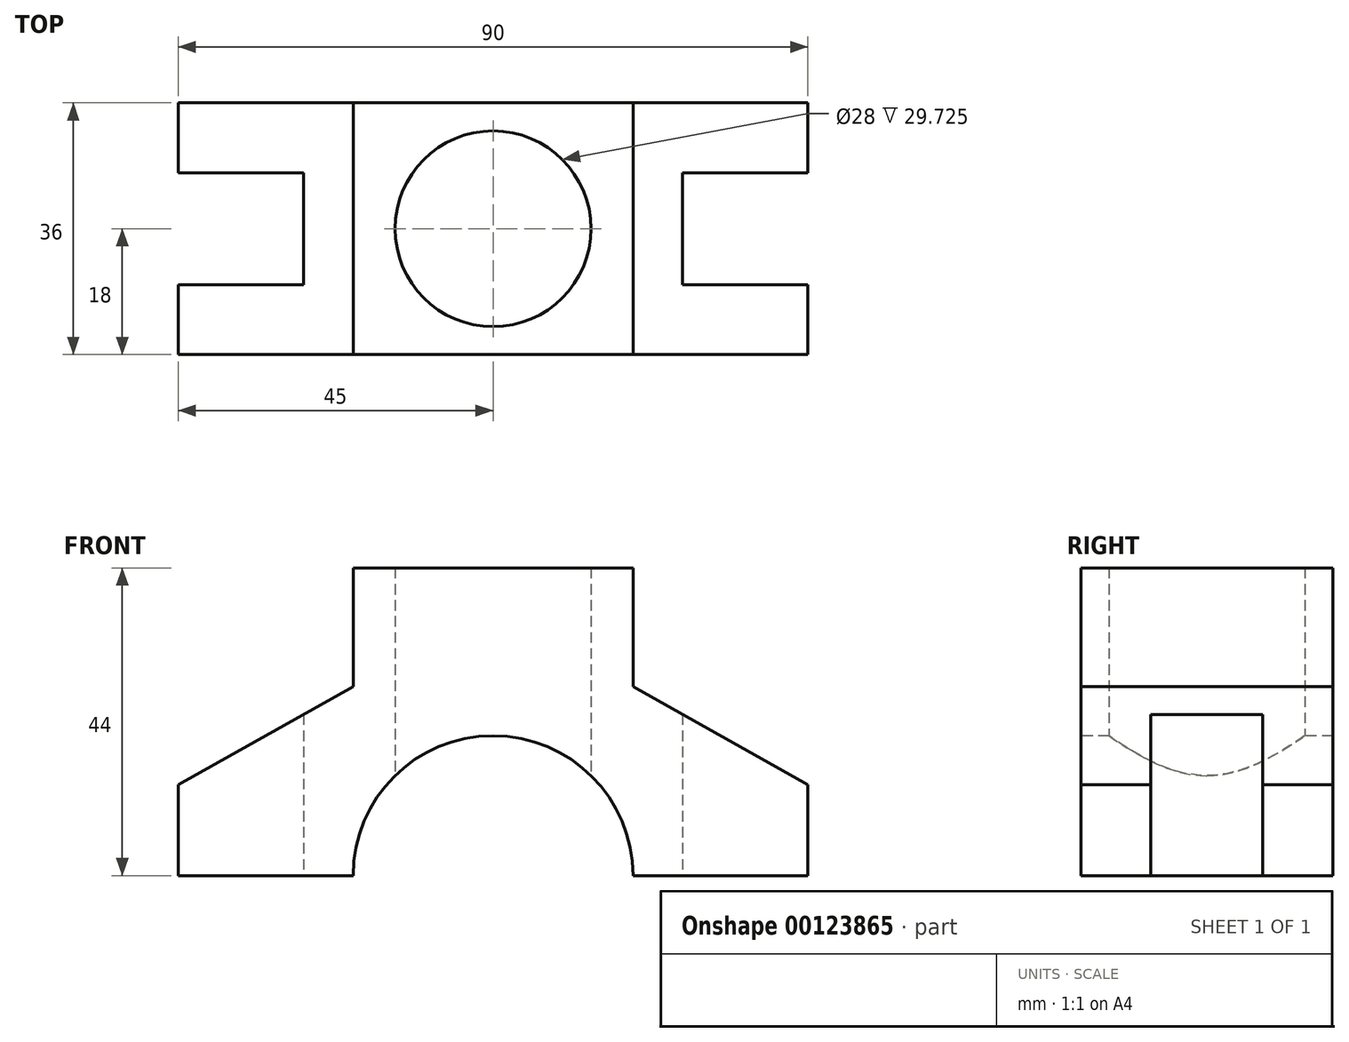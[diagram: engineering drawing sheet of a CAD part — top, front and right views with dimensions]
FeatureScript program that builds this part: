
annotation { "Feature Type Name" : "Feature", "Feature Type Description" : "" }
export const myFeature = defineFeature(function(context is Context, id is Id, definition is map)
    precondition{}
    {
        {
            var Q0;
            Q0=qCreatedBy(makeId("Front.planeOp"),FACE);
            var sketch = newSketch(context, id + "F0", { "sketchPlane" : qUnion([Q0])});
            skLineSegment(sketch, "E0", {"start": v(0, 0) * mm, "end": v(-45, 0) * mm});
            skLineSegment(sketch, "E1", {"start": v(-45, 0) * mm, "end": v(-45, 13) * mm});
            skLineSegment(sketch, "E2", {"start": v(0, 0) * mm, "end": v(0, 44) * mm});
            skLineSegment(sketch, "E3", {"start": v(0, 44) * mm, "end": v(-20, 44) * mm});
            skLineSegment(sketch, "E4", {"start": v(-20, 44) * mm, "end": v(-20, 27) * mm});
            skLineSegment(sketch, "E5", {"start": v(-20, 27) * mm, "end": v(-45, 13) * mm});
            skLineSegment(sketch, "E6.MirrorCS", {"start": v(0, 0) * mm, "end": v(45, 0) * mm});
            skLineSegment(sketch, "E7.MirrorCS", {"start": v(0, 44) * mm, "end": v(20, 44) * mm});
            skLineSegment(sketch, "E8.MirrorCS", {"start": v(45, 0) * mm, "end": v(45, 13) * mm});
            skLineSegment(sketch, "E9.MirrorCS", {"start": v(20, 27) * mm, "end": v(45, 13) * mm});
            skLineSegment(sketch, "E10.MirrorCS", {"start": v(20, 44) * mm, "end": v(20, 27) * mm});
            skSolve(sketch);
        }
        {
            var Q0;
            Q0=makeQuery(id+"F0.imprint","IMPRINT",FACE,{"disambiguationData":[TD([[makeQuery(id+"F0.imprint","IMPRINT",EDGE,{"derivedFrom":sQuery(id+"F0.wireOp",EDGE,"E2")}),-1.0]])]});
            var Q1;
            Q1=makeQuery(id+"F0.imprint","IMPRINT",FACE,{"disambiguationData":[TD([[makeQuery(id+"F0.imprint","IMPRINT",EDGE,{"derivedFrom":sQuery(id+"F0.wireOp",EDGE,"E0")}),-1.0]])]});
            extrude(context, id + "F1", {"entities" : qUnion([Q0, Q1]), "oppositeDirection" : true, "depth" : 36 * mm});
        }
        {
            var Q0;
            Q0=makeQuery(id+"F1.opExtrude","CAP_FACE",FACE,{"disambiguationData":[OSD([sQuery(id+"F0.wireOp",EDGE,"E0"),sQuery(id+"F0.wireOp",EDGE,"E1"),sQuery(id+"F0.wireOp",EDGE,"E3"),sQuery(id+"F0.wireOp",EDGE,"E4"),sQuery(id+"F0.wireOp",EDGE,"E5"),sQuery(id+"F0.wireOp",EDGE,"E6.MirrorCS"),sQuery(id+"F0.wireOp",EDGE,"E7.MirrorCS"),sQuery(id+"F0.wireOp",EDGE,"E8.MirrorCS"),sQuery(id+"F0.wireOp",EDGE,"E9.MirrorCS"),sQuery(id+"F0.wireOp",EDGE,"E10.MirrorCS")])],"isStart":true});
            var sketch = newSketch(context, id + "F2", { "sketchPlane" : qUnion([Q0])});
            skCircle(sketch, "E11", {"center": v(0, 0) * mm, "radius": 20 * mm});
            skSolve(sketch);
        }
        {
            var Q0;
            {var subQ0=sQuery(id+"F2.wireOp",EDGE,"E11");var subQ1=makeQuery(id+"F1.opExtrude","CAP_EDGE",EDGE,{"disambiguationData":[OSD([sQuery(id+"F0.wireOp",EDGE,"E0"),sQuery(id+"F0.wireOp",EDGE,"E6.MirrorCS")])],"isStart":true});var subQ2=makeQuery(id+"F2.imprint","INTERSECT",VERTEX,{"disambiguationData":[OD(0.0)],"derivedFrom":[subQ1,subQ0]});Q0=makeQuery(id+"F2.imprint","IMPRINT",FACE,{"disambiguationData":[TD([[makeQuery(id+"F2.imprint","IMPRINT",EDGE,{"disambiguationData":[TD([[subQ2,1.0]])],"derivedFrom":subQ0}),1.0]])]});}
            extrude(context, id + "F3", {"entities" : qUnion([Q0]), "operationType" : NewBodyOperationType.REMOVE, "oppositeDirection" : true, "depth" : 36 * mm});
        }
        {
            var Q0;
            Q0=qCreatedBy(makeId("Top.planeOp"),FACE);
            var sketch = newSketch(context, id + "F4", { "sketchPlane" : qUnion([Q0])});
            skCircle(sketch, "E12", {"center": v(0, 18) * mm, "radius": 14 * mm});
            skLineSegment(sketch, "E13", {"start": v(-45.06, 10) * mm, "end": v(-45.06, 26) * mm});
            skLineSegment(sketch, "E14", {"start": v(-45.06, 26) * mm, "end": v(-27.06, 26) * mm});
            skLineSegment(sketch, "E15", {"start": v(-27.06, 26) * mm, "end": v(-27.06, 10) * mm});
            skLineSegment(sketch, "E16", {"start": v(-27.06, 10) * mm, "end": v(-45.06, 10) * mm});
            skLineSegment(sketch, "E17.MirrorCS", {"start": v(27.06, 26) * mm, "end": v(27.06, 10) * mm});
            skLineSegment(sketch, "E18.MirrorCS", {"start": v(45.06, 26) * mm, "end": v(27.06, 26) * mm});
            skLineSegment(sketch, "E19.MirrorCS", {"start": v(45.06, 10) * mm, "end": v(45.06, 26) * mm});
            skLineSegment(sketch, "E20.MirrorCS", {"start": v(27.06, 10) * mm, "end": v(45.06, 10) * mm});
            skSolve(sketch);
        }
        {
            var Q0;
            Q0 = qSketchRegion(id + "F4", true);
            extrude(context, id + "F5", {"entities" : qUnion([Q0]), "operationType" : NewBodyOperationType.REMOVE, "depth" : 44 * mm});
        }
    });
